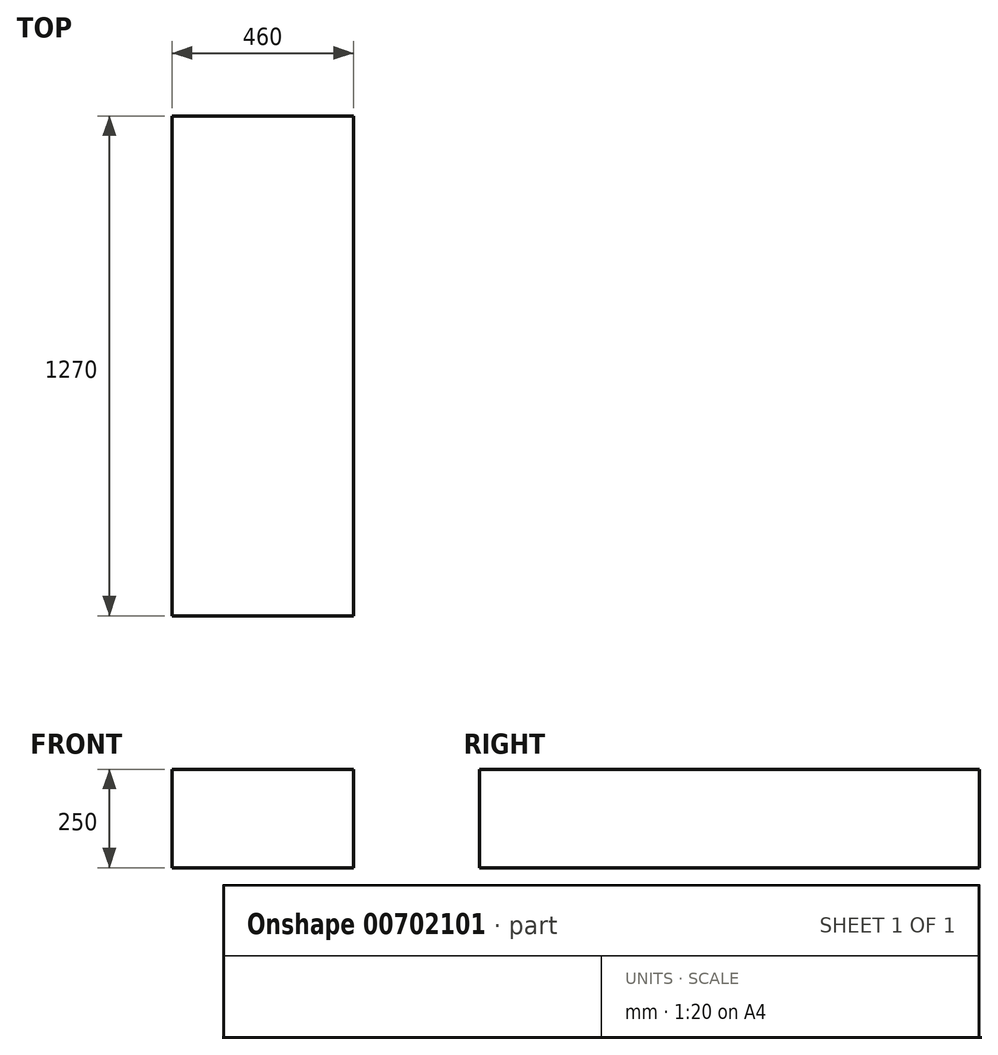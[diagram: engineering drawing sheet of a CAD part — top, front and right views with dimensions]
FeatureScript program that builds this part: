
annotation { "Feature Type Name" : "Feature", "Feature Type Description" : "" }
export const myFeature = defineFeature(function(context is Context, id is Id, definition is map)
    precondition{}
    {
        {
            var Q0;
            Q0=qCreatedBy(makeId("Top.planeOp"),FACE);
            var sketch = newSketch(context, id + "F0", { "sketchPlane" : qUnion([Q0])});
            skLineSegment(sketch, "E0.bottom", {"start": v(0, 0) * mm, "end": v(460, 0) * mm});
            skLineSegment(sketch, "E0.top", {"start": v(0, 1270) * mm, "end": v(460, 1270) * mm});
            skLineSegment(sketch, "E0.left", {"start": v(0, 0) * mm, "end": v(0, 1270) * mm});
            skLineSegment(sketch, "E0.right", {"start": v(460, 0) * mm, "end": v(460, 1270) * mm});
            skSolve(sketch);
        }
        {
            var Q0;
            Q0 = qSketchRegion(id + "F0", true);
            extrude(context, id + "F1", {"entities" : qUnion([Q0]), "depth" : 250 * mm, "offsetDistance" : 25 * mm});
        }
    });
